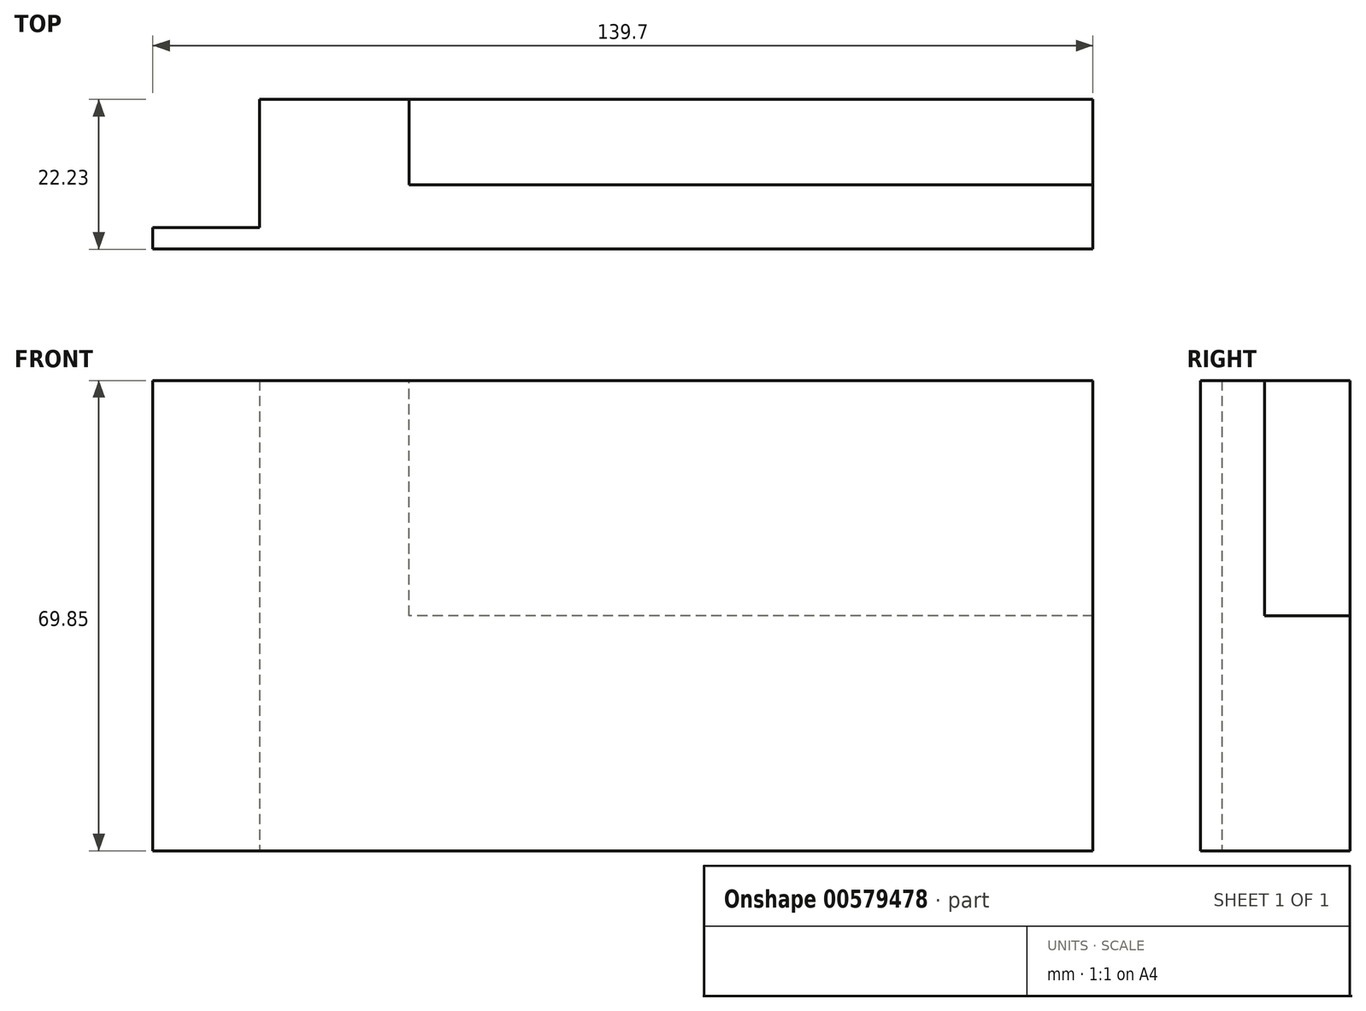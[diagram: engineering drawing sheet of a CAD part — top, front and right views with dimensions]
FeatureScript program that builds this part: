
annotation { "Feature Type Name" : "Feature", "Feature Type Description" : "" }
export const myFeature = defineFeature(function(context is Context, id is Id, definition is map)
    precondition{}
    {
        {
            var Q0;
            Q0=qCreatedBy(makeId("Front.planeOp"),FACE);
            var sketch = newSketch(context, id + "F0", { "sketchPlane" : qUnion([Q0])});
            skLineSegment(sketch, "E0", {"start": v(-63.95, 0) * mm, "end": v(-63.95, 69.85) * mm});
            skLineSegment(sketch, "E1", {"start": v(-63.95, 69.85) * mm, "end": v(75.75, 69.85) * mm});
            skLineSegment(sketch, "E2", {"start": v(75.75, 69.85) * mm, "end": v(75.75, 0) * mm});
            skLineSegment(sketch, "E3", {"start": v(75.75, 0) * mm, "end": v(-63.95, 0) * mm});
            skSolve(sketch);
        }
        {
            var Q0;
            Q0=makeQuery(id+"F0.imprint","IMPRINT",FACE,{"disambiguationData":[TD([[makeQuery(id+"F0.imprint","IMPRINT",EDGE,{"derivedFrom":sQuery(id+"F0.wireOp",EDGE,"E0")}),-1.0]])]});
            extrude(context, id + "F1", {"entities" : qUnion([Q0]), "depth" : 22.22 * mm, "offsetDistance" : 25.4 * mm});
        }
        {
            var Q0;
            Q0=qCreatedBy(makeId("Front.planeOp"),FACE);
            var sketch = newSketch(context, id + "F2", { "sketchPlane" : qUnion([Q0])});
            skLineSegment(sketch, "E4.bottom", {"start": v(75.75, 34.93) * mm, "end": v(-25.85, 34.93) * mm});
            skLineSegment(sketch, "E4.top", {"start": v(75.75, 69.85) * mm, "end": v(-25.85, 69.85) * mm});
            skLineSegment(sketch, "E4.left", {"start": v(75.75, 34.93) * mm, "end": v(75.75, 69.85) * mm});
            skLineSegment(sketch, "E4.right", {"start": v(-25.85, 34.92) * mm, "end": v(-25.85, 69.85) * mm});
            skSolve(sketch);
        }
        {
            var Q0;
            Q0=makeQuery(id+"F2.imprint","IMPRINT",FACE,{"disambiguationData":[TD([[makeQuery(id+"F2.imprint","IMPRINT",EDGE,{"derivedFrom":sQuery(id+"F2.wireOp",EDGE,"E4.bottom")}),-1.0]])]});
            extrude(context, id + "F3", {"entities" : qUnion([Q0]), "operationType" : NewBodyOperationType.REMOVE, "depth" : 12.7 * mm, "offsetDistance" : 25.4 * mm});
        }
        {
            var Q0;
            Q0=qCreatedBy(makeId("Front.planeOp"),FACE);
            var sketch = newSketch(context, id + "F4", { "sketchPlane" : qUnion([Q0])});
            skLineSegment(sketch, "E5.bottom", {"start": v(-48.07, 69.85) * mm, "end": v(-63.95, 69.85) * mm});
            skLineSegment(sketch, "E5.top", {"start": v(-48.07, 0) * mm, "end": v(-63.95, 0) * mm});
            skLineSegment(sketch, "E5.left", {"start": v(-48.07, 69.85) * mm, "end": v(-48.07, 0) * mm});
            skLineSegment(sketch, "E5.right", {"start": v(-63.95, 69.85) * mm, "end": v(-63.95, 0) * mm});
            skSolve(sketch);
        }
        {
            var Q0;
            Q0 = qSketchRegion(id + "F4", true);
            extrude(context, id + "F5", {"entities" : qUnion([Q0]), "operationType" : NewBodyOperationType.REMOVE, "depth" : 19.05 * mm, "offsetDistance" : 25.4 * mm});
        }
    });
